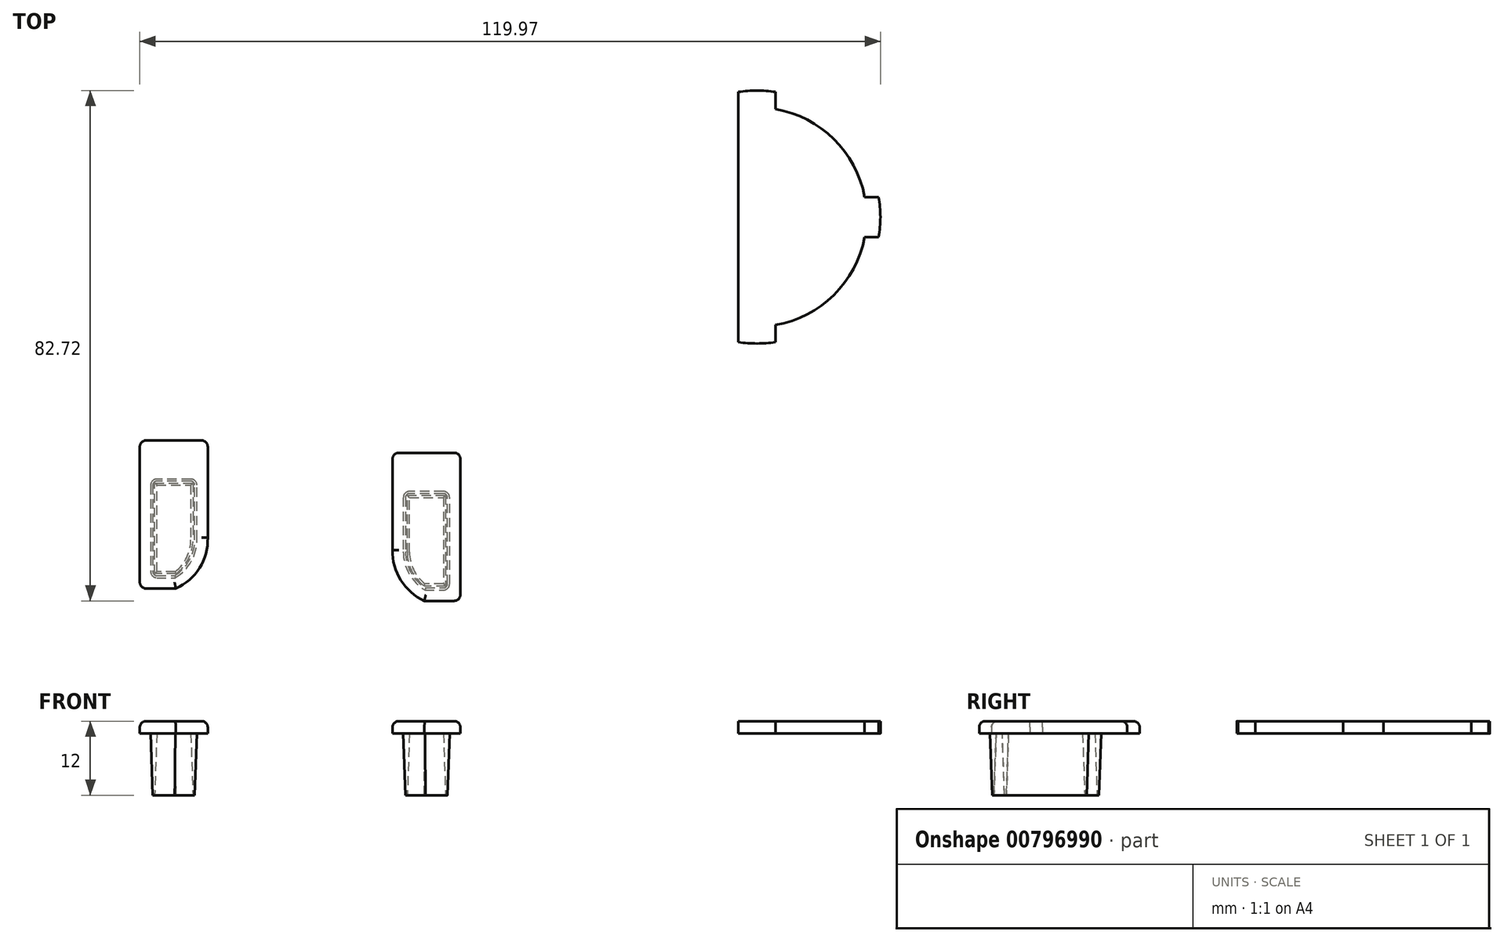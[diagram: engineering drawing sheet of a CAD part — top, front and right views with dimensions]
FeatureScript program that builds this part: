
annotation { "Feature Type Name" : "Feature", "Feature Type Description" : "" }
export const myFeature = defineFeature(function(context is Context, id is Id, definition is map)
    precondition{}
    {
        {
            var Q0;
            Q0=qCreatedBy(makeId("Top.planeOp"),FACE);
            var sketch = newSketch(context, id + "F0", { "sketchPlane" : qUnion([Q0])});
            skArc(sketch, "E0", {"start": v(3, -17.5) * mm, "mid": v(12.46, -12.64) * mm, "end": v(17.45, -3.25) * mm});
            skArc(sketch, "E1", {"start": v(-3, -20.28) * mm, "mid": v(0, -20.5) * mm, "end": v(3, -20.28) * mm});
            skLineSegment(sketch, "E2", {"start": v(-3, 20.28) * mm, "end": v(-3, -20.28) * mm});
            skLineSegment(sketch, "E3", {"start": v(3, -20.28) * mm, "end": v(3, -17.5) * mm});
            skPoint(sketch, "E4.start.orphan", {"position": v(0, 24.86) * mm});
            skLineSegment(sketch, "E5.trimOffspring", {"start": v(3, 17.5) * mm, "end": v(3, 20.28) * mm});
            skLineSegment(sketch, "E6", {"start": v(17.45, -3.25) * mm, "end": v(19.73, -3.25) * mm});
            skLineSegment(sketch, "E7", {"start": v(17.45, 3.25) * mm, "end": v(19.73, 3.25) * mm});
            skArc(sketch, "E8", {"start": v(19.73, -3.25) * mm, "mid": v(20, 0) * mm, "end": v(19.73, 3.25) * mm});
            skArc(sketch, "E9.trimOffspring", {"start": v(3, 20.28) * mm, "mid": v(0, 20.5) * mm, "end": v(-3, 20.28) * mm});
            skPoint(sketch, "E10.orphan", {"position": v(22.7, 0) * mm});
            skPoint(sketch, "E11.orphan", {"position": v(11.98, 0) * mm});
            skArc(sketch, "E12.trimOffspring", {"start": v(17.45, 3.25) * mm, "mid": v(12.46, 12.64) * mm, "end": v(3, 17.5) * mm});
            skSolve(sketch);
        }
        {
            var Q0;
            Q0 = qSketchRegion(id + "F0", true);
            extrude(context, id + "F1", {"entities" : qUnion([Q0]), "depth" : 2 * mm, "offsetDistance" : 25 * mm});
        }
        {
            var Q0;
            Q0=qCreatedBy(makeId("Top.planeOp"),FACE);
            var sketch = newSketch(context, id + "F2", { "sketchPlane" : qUnion([Q0])});
            skLineSegment(sketch, "E13.bottom", {"start": v(-94.22, -58.47) * mm, "end": v(-97.22, -58.47) * mm});
            skLineSegment(sketch, "E13.top", {"start": v(-91.72, -42.47) * mm, "end": v(-97.22, -42.47) * mm});
            skLineSegment(sketch, "E13.left", {"start": v(-90.72, -52.25) * mm, "end": v(-90.72, -43.47) * mm});
            skLineSegment(sketch, "E13.right", {"start": v(-98.22, -57.47) * mm, "end": v(-98.22, -43.47) * mm});
            skPoint(sketch, "E13.middle", {"position": v(-94.22, -50.22) * mm});
            skArc(sketch, "E14", {"start": v(-94.22, -58.47) * mm, "mid": v(-91.65, -55.82) * mm, "end": v(-90.72, -52.25) * mm});
            skLineSegment(sketch, "E15.0", {"start": v(-99.97, -59.22) * mm, "end": v(-99.97, -41.47) * mm});
            skLineSegment(sketch, "E15.2", {"start": v(-94.13, -60.22) * mm, "end": v(-98.97, -60.22) * mm});
            skArc(sketch, "E15.3", {"start": v(-94.13, -60.22) * mm, "mid": v(-90.3, -56.88) * mm, "end": v(-88.97, -51.97) * mm});
            skLineSegment(sketch, "E15.4", {"start": v(-88.97, -51.97) * mm, "end": v(-88.97, -41.47) * mm});
            skPoint(sketch, "E16.visualSharp", {"position": v(-99.97, -40.47) * mm});
            skPoint(sketch, "E17.visualSharp", {"position": v(-99.97, -60.22) * mm});
            skArc(sketch, "E17.filletArc", {"start": v(-99.97, -59.22) * mm, "mid": v(-99.67, -59.93) * mm, "end": v(-98.97, -60.22) * mm});
            skPoint(sketch, "E18.visualSharp", {"position": v(-98.22, -58.47) * mm});
            skArc(sketch, "E18.filletArc", {"start": v(-98.22, -57.47) * mm, "mid": v(-97.92, -58.18) * mm, "end": v(-97.22, -58.47) * mm});
            skPoint(sketch, "E19.visualSharp", {"position": v(-88.97, -40.47) * mm});
            skPoint(sketch, "E20.visualSharp", {"position": v(-90.72, -42.47) * mm});
            skArc(sketch, "E20.filletArc", {"start": v(-90.72, -43.47) * mm, "mid": v(-91, -42.76) * mm, "end": v(-91.72, -42.47) * mm});
            skPoint(sketch, "E21.visualSharp", {"position": v(-98.22, -42.47) * mm});
            skArc(sketch, "E21.filletArc", {"start": v(-97.22, -42.47) * mm, "mid": v(-97.92, -42.76) * mm, "end": v(-98.22, -43.47) * mm});
            skLineSegment(sketch, "E22", {"start": v(-98.97, -36.22) * mm, "end": v(-89.97, -36.22) * mm});
            skLineSegment(sketch, "E23", {"start": v(-99.97, -41.47) * mm, "end": v(-99.97, -37.22) * mm});
            skLineSegment(sketch, "E24", {"start": v(-88.97, -41.47) * mm, "end": v(-88.97, -37.22) * mm});
            skPoint(sketch, "E25.visualSharp", {"position": v(-99.97, -36.22) * mm});
            skArc(sketch, "E25.filletArc", {"start": v(-98.97, -36.22) * mm, "mid": v(-99.67, -36.51) * mm, "end": v(-99.97, -37.22) * mm});
            skPoint(sketch, "E26.visualSharp", {"position": v(-88.97, -36.22) * mm});
            skArc(sketch, "E26.filletArc", {"start": v(-88.97, -37.22) * mm, "mid": v(-89.26, -36.51) * mm, "end": v(-89.97, -36.22) * mm});
            skPoint(sketch, "E27.start.orphan", {"position": v(-98.22, -51.97) * mm});
            skLineSegment(sketch, "E28", {"start": v(-97.22, -43.47) * mm, "end": v(-91.72, -43.47) * mm});
            skLineSegment(sketch, "E29", {"start": v(-91.72, -52.32) * mm, "end": v(-91.72, -43.47) * mm});
            skLineSegment(sketch, "E30", {"start": v(-97.22, -43.47) * mm, "end": v(-97.22, -57.47) * mm});
            skLineSegment(sketch, "E31", {"start": v(-94.22, -57.47) * mm, "end": v(-97.22, -57.47) * mm});
            skArc(sketch, "E32", {"start": v(-94.22, -57.47) * mm, "mid": v(-92.37, -55.18) * mm, "end": v(-91.72, -52.32) * mm});
            skPoint(sketch, "E33.orphan", {"position": v(-94.47, -52.1) * mm});
            skLineSegment(sketch, "E34.MirrorCS", {"start": v(-56.28, -44.47) * mm, "end": v(-50.78, -44.47) * mm});
            skArc(sketch, "E35.MirrorCS", {"start": v(-50.78, -44.47) * mm, "mid": v(-50.08, -44.76) * mm, "end": v(-49.78, -45.47) * mm});
            skArc(sketch, "E36.MirrorCS", {"start": v(-57.28, -45.47) * mm, "mid": v(-57, -44.76) * mm, "end": v(-56.28, -44.47) * mm});
            skLineSegment(sketch, "E37.MirrorCS", {"start": v(-50.78, -45.47) * mm, "end": v(-56.28, -45.47) * mm});
            skLineSegment(sketch, "E38.MirrorCS", {"start": v(-53.78, -59.47) * mm, "end": v(-50.78, -59.47) * mm});
            skArc(sketch, "E39.MirrorCS", {"start": v(-48.03, -61.22) * mm, "mid": v(-48.33, -61.93) * mm, "end": v(-49.03, -62.22) * mm});
            skArc(sketch, "E40.MirrorCS", {"start": v(-49.78, -59.47) * mm, "mid": v(-50.08, -60.18) * mm, "end": v(-50.78, -60.47) * mm});
            skLineSegment(sketch, "E41.MirrorCS", {"start": v(-53.87, -62.22) * mm, "end": v(-49.03, -62.22) * mm});
            skLineSegment(sketch, "E42.MirrorCS", {"start": v(-53.78, -60.47) * mm, "end": v(-50.78, -60.47) * mm});
            skArc(sketch, "E43.MirrorCS", {"start": v(-59.03, -39.22) * mm, "mid": v(-58.74, -38.51) * mm, "end": v(-58.03, -38.22) * mm});
            skLineSegment(sketch, "E44.MirrorCS", {"start": v(-59.03, -43.47) * mm, "end": v(-59.03, -39.22) * mm});
            skArc(sketch, "E45.MirrorCS", {"start": v(-49.03, -38.22) * mm, "mid": v(-48.33, -38.51) * mm, "end": v(-48.03, -39.22) * mm});
            skArc(sketch, "E46.MirrorCS", {"start": v(-53.78, -60.47) * mm, "mid": v(-56.35, -57.82) * mm, "end": v(-57.28, -54.25) * mm});
            skArc(sketch, "E47.MirrorCS", {"start": v(-53.78, -59.47) * mm, "mid": v(-55.63, -57.18) * mm, "end": v(-56.28, -54.32) * mm});
            skLineSegment(sketch, "E48.MirrorCS", {"start": v(-48.03, -43.47) * mm, "end": v(-48.03, -39.22) * mm});
            skLineSegment(sketch, "E49.MirrorCS", {"start": v(-50.78, -45.47) * mm, "end": v(-50.78, -59.47) * mm});
            skLineSegment(sketch, "E50.MirrorCS", {"start": v(-56.28, -54.32) * mm, "end": v(-56.28, -45.47) * mm});
            skLineSegment(sketch, "E51.MirrorCS", {"start": v(-57.28, -54.25) * mm, "end": v(-57.28, -45.47) * mm});
            skLineSegment(sketch, "E52.MirrorCS", {"start": v(-48.03, -61.22) * mm, "end": v(-48.03, -43.47) * mm});
            skArc(sketch, "E53.MirrorCS", {"start": v(-53.87, -62.22) * mm, "mid": v(-57.7, -58.88) * mm, "end": v(-59.03, -53.97) * mm});
            skLineSegment(sketch, "E54.MirrorCS", {"start": v(-49.03, -38.22) * mm, "end": v(-58.03, -38.22) * mm});
            skLineSegment(sketch, "E55.MirrorCS", {"start": v(-59.03, -53.97) * mm, "end": v(-59.03, -43.47) * mm});
            skLineSegment(sketch, "E56.MirrorCS", {"start": v(-49.78, -59.47) * mm, "end": v(-49.78, -45.47) * mm});
            skPoint(sketch, "E57.MirrorP", {"position": v(-53.78, -52.22) * mm});
            skPoint(sketch, "E58.MirrorP", {"position": v(-49.78, -53.97) * mm});
            skPoint(sketch, "E59.MirrorP", {"position": v(-59.03, -38.22) * mm});
            skPoint(sketch, "E60.MirrorP", {"position": v(-48.03, -42.47) * mm});
            skPoint(sketch, "E61.MirrorP", {"position": v(-53.53, -54.1) * mm});
            skPoint(sketch, "E62.MirrorP", {"position": v(-59.03, -42.47) * mm});
            skPoint(sketch, "E63.MirrorP", {"position": v(-57.28, -44.47) * mm});
            skPoint(sketch, "E64.MirrorP", {"position": v(-49.78, -44.47) * mm});
            skPoint(sketch, "E65.MirrorP", {"position": v(-48.03, -62.22) * mm});
            skPoint(sketch, "E66.MirrorP", {"position": v(-48.03, -38.22) * mm});
            skPoint(sketch, "E67.MirrorP", {"position": v(-49.78, -60.47) * mm});
            skSolve(sketch);
        }
        {
            var Q0;
            Q0=makeQuery(id+"F2.imprint","IMPRINT",FACE,{"disambiguationData":[TD([[makeQuery(id+"F2.imprint","IMPRINT",EDGE,{"derivedFrom":sQuery(id+"F2.wireOp",EDGE,"E13.bottom")}),1.0]])]});
            var Q1;
            Q1=makeQuery(id+"F2.imprint","IMPRINT",FACE,{"disambiguationData":[TD([[makeQuery(id+"F2.imprint","IMPRINT",EDGE,{"derivedFrom":sQuery(id+"F2.wireOp",EDGE,"E13.bottom")}),-1.0]])]});
            var Q2;
            Q2=makeQuery(id+"F2.imprint","IMPRINT",FACE,{"disambiguationData":[TD([[makeQuery(id+"F2.imprint","IMPRINT",EDGE,{"derivedFrom":sQuery(id+"F2.wireOp",EDGE,"E28")}),-1.0]])]});
            var Q3;
            Q3=makeQuery(id+"F2.imprint","IMPRINT",FACE,{"disambiguationData":[TD([[makeQuery(id+"F2.imprint","IMPRINT",EDGE,{"derivedFrom":sQuery(id+"F2.wireOp",EDGE,"E34.MirrorCS")}),1.0]])]});
            var Q4;
            Q4=makeQuery(id+"F2.imprint","IMPRINT",FACE,{"disambiguationData":[TD([[makeQuery(id+"F2.imprint","IMPRINT",EDGE,{"derivedFrom":sQuery(id+"F2.wireOp",EDGE,"E34.MirrorCS")}),-1.0]])]});
            var Q5;
            Q5=makeQuery(id+"F2.imprint","IMPRINT",FACE,{"disambiguationData":[TD([[makeQuery(id+"F2.imprint","IMPRINT",EDGE,{"derivedFrom":sQuery(id+"F2.wireOp",EDGE,"E37.MirrorCS")}),1.0]])]});
            extrude(context, id + "F3", {"entities" : qUnion([Q0, Q1, Q2, Q3, Q4, Q5]), "depth" : 2 * mm, "offsetDistance" : 25 * mm});
        }
        {
            var Q0;
            Q0=makeQuery(id+"F2.imprint","IMPRINT",FACE,{"disambiguationData":[TD([[makeQuery(id+"F2.imprint","IMPRINT",EDGE,{"derivedFrom":sQuery(id+"F2.wireOp",EDGE,"E13.bottom")}),-1.0]])]});
            var Q1;
            Q1=makeQuery(id+"F2.imprint","IMPRINT",FACE,{"disambiguationData":[TD([[makeQuery(id+"F2.imprint","IMPRINT",EDGE,{"derivedFrom":sQuery(id+"F2.wireOp",EDGE,"E34.MirrorCS")}),-1.0]])]});
            extrude(context, id + "F4", {"entities" : qUnion([Q0, Q1]), "oppositeDirection" : true, "depth" : 10 * mm, "offsetDistance" : 25 * mm, "hasDraft" : true, "draftAngle" : 2 * degree, "draftPullDirection" : true});
        }
        {
            var Q0;
            Q0=makeQuery(id+"F3.opExtrude","CAP_FACE",FACE,{"disambiguationData":[OSD([sQuery(id+"F2.wireOp",EDGE,"E15.0"),sQuery(id+"F2.wireOp",EDGE,"E15.2"),sQuery(id+"F2.wireOp",EDGE,"E15.3"),sQuery(id+"F2.wireOp",EDGE,"E15.4"),sQuery(id+"F2.wireOp",EDGE,"E17.filletArc"),sQuery(id+"F2.wireOp",EDGE,"E22"),sQuery(id+"F2.wireOp",EDGE,"E23"),sQuery(id+"F2.wireOp",EDGE,"E24"),sQuery(id+"F2.wireOp",EDGE,"E25.filletArc"),sQuery(id+"F2.wireOp",EDGE,"E26.filletArc")])],"isStart":false});
            var Q1;
            Q1=makeQuery(id+"F3.opExtrude","CAP_FACE",FACE,{"disambiguationData":[OSD([sQuery(id+"F2.wireOp",EDGE,"E39.MirrorCS"),sQuery(id+"F2.wireOp",EDGE,"E41.MirrorCS"),sQuery(id+"F2.wireOp",EDGE,"E43.MirrorCS"),sQuery(id+"F2.wireOp",EDGE,"E44.MirrorCS"),sQuery(id+"F2.wireOp",EDGE,"E45.MirrorCS"),sQuery(id+"F2.wireOp",EDGE,"E48.MirrorCS"),sQuery(id+"F2.wireOp",EDGE,"E52.MirrorCS"),sQuery(id+"F2.wireOp",EDGE,"E53.MirrorCS"),sQuery(id+"F2.wireOp",EDGE,"E54.MirrorCS"),sQuery(id+"F2.wireOp",EDGE,"E55.MirrorCS")])],"isStart":false});
            fillet(context, id + "F5", {"entities" : qUnion([Q0, Q1]), "radius" : 1 * mm, "tangentPropagation" : true, "allowEdgeOverflow" : false});
        }
    });
